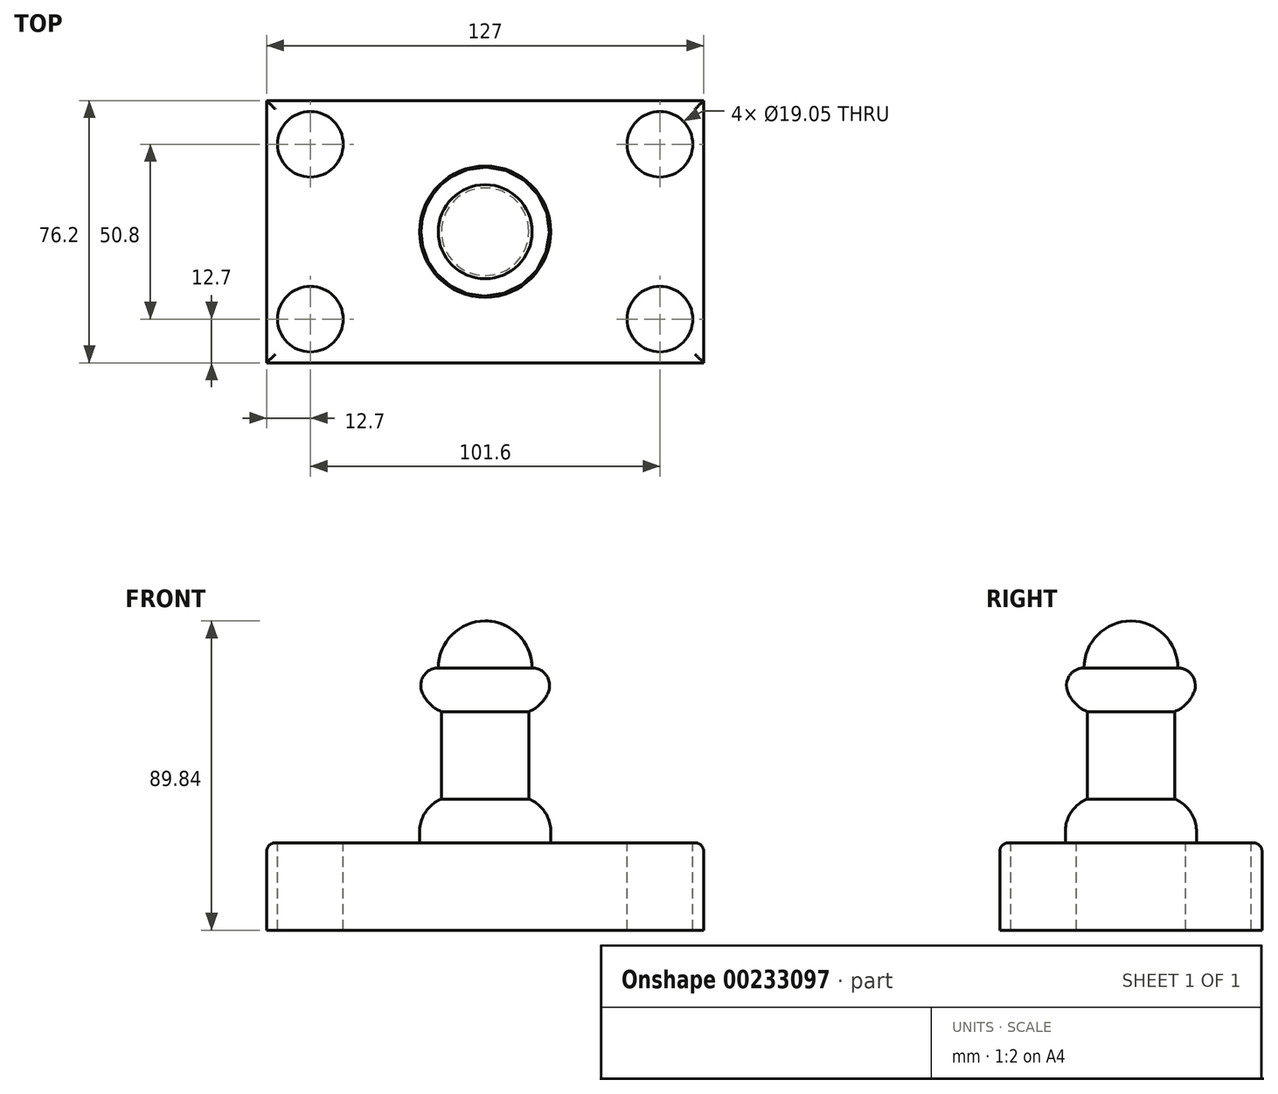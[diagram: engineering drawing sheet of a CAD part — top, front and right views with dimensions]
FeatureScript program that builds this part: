
annotation { "Feature Type Name" : "Feature", "Feature Type Description" : "" }
export const myFeature = defineFeature(function(context is Context, id is Id, definition is map)
    precondition{}
    {
        {
            var Q0;
            Q0=qCreatedBy(makeId("Top.planeOp"),FACE);
            var sketch = newSketch(context, id + "F0", { "sketchPlane" : qUnion([Q0])});
            skLineSegment(sketch, "E0.bottom", {"start": v(63.5, 38.1) * mm, "end": v(-63.5, 38.1) * mm});
            skLineSegment(sketch, "E0.top", {"start": v(63.5, -38.1) * mm, "end": v(-63.5, -38.1) * mm});
            skLineSegment(sketch, "E0.left", {"start": v(63.5, 38.1) * mm, "end": v(63.5, -38.1) * mm});
            skLineSegment(sketch, "E0.right", {"start": v(-63.5, 38.1) * mm, "end": v(-63.5, -38.1) * mm});
            skPoint(sketch, "E0.middle", {"position": v(0, 0) * mm});
            skSolve(sketch);
        }
        {
            var Q0;
            Q0=makeQuery(id+"F0.imprint","IMPRINT",FACE,{"disambiguationData":[TD([[makeQuery(id+"F0.imprint","IMPRINT",EDGE,{"derivedFrom":sQuery(id+"F0.wireOp",EDGE,"E0.bottom")}),1.0]])]});
            extrude(context, id + "F1", {"entities" : qUnion([Q0]), "depth" : 25.4 * mm});
        }
        {
            var Q0;
            Q0=makeQuery(id+"F1.opExtrude","CAP_FACE",FACE,{"disambiguationData":[OSD([sQuery(id+"F0.wireOp",EDGE,"E0.bottom"),sQuery(id+"F0.wireOp",EDGE,"E0.top"),sQuery(id+"F0.wireOp",EDGE,"E0.left"),sQuery(id+"F0.wireOp",EDGE,"E0.right")])],"isStart":false});
            var sketch = newSketch(context, id + "F2", { "sketchPlane" : qUnion([Q0])});
            skCircle(sketch, "E1", {"center": v(-50.8, 25.4) * mm, "radius": 9.53 * mm});
            skCircle(sketch, "E2", {"center": v(50.8, 25.4) * mm, "radius": 9.53 * mm});
            skCircle(sketch, "E3", {"center": v(50.8, -25.4) * mm, "radius": 9.53 * mm});
            skCircle(sketch, "E4", {"center": v(-50.8, -25.4) * mm, "radius": 9.53 * mm});
            skSolve(sketch);
        }
        {
            var Q0;
            Q0=sQuery(id+"F2.wireOp",VERTEX,"E1.center");
            var Q1;
            Q1=sQuery(id+"F2.wireOp",VERTEX,"E2.center");
            var Q2;
            Q2=sQuery(id+"F2.wireOp",VERTEX,"E4.center");
            var Q3;
            Q3=sQuery(id+"F2.wireOp",VERTEX,"E3.center");
            var Q4;
            Q4=makeQuery(id+"F1.opExtrude","SWEPT_BODY",BODY,{"disambiguationData":[OSD([sQuery(id+"F0.wireOp",EDGE,"E0.bottom"),sQuery(id+"F0.wireOp",EDGE,"E0.top"),sQuery(id+"F0.wireOp",EDGE,"E0.left"),sQuery(id+"F0.wireOp",EDGE,"E0.right")])]});
            hole(context, id + "F3", {"style" : HoleStyle.SIMPLE, "endStyle" : HoleEndStyle.THROUGH, "holeDiameter" : 19.05 * mm, "locations" : qUnion([Q0, Q1, Q2, Q3]), "scope" : qUnion([Q4]), "isTappedThrough" : true});
        }
        {
            var Q0;
            Q0=qCreatedBy(makeId("Front.planeOp"),FACE);
            var sketch = newSketch(context, id + "F4", { "sketchPlane" : qUnion([Q0])});
            skLineSegment(sketch, "E5.bottom", {"start": v(0, 25.4) * mm, "end": v(-19.05, 25.4) * mm});
            skLineSegment(sketch, "E5.top", {"start": v(0, 76.2) * mm, "end": v(-19.05, 76.2) * mm});
            skLineSegment(sketch, "E5.left", {"start": v(0, 25.4) * mm, "end": v(0, 76.2) * mm});
            skLineSegment(sketch, "E5.right", {"start": v(-19.05, 25.4) * mm, "end": v(-19.05, 76.2) * mm});
            skSolve(sketch);
        }
        {
            var Q0;
            Q0=makeQuery(id+"F4.imprint","IMPRINT",FACE,{"disambiguationData":[TD([[makeQuery(id+"F4.imprint","IMPRINT",EDGE,{"derivedFrom":sQuery(id+"F4.wireOp",EDGE,"E5.bottom")}),-1.0]])]});
            var Q1;
            Q1=sQuery(id+"F4.wireOp",EDGE,"E5.left");
            revolve(context, id + "F5", {"operationType" : NewBodyOperationType.ADD, "entities" : qUnion([Q0]), "axis" : qUnion([Q1]), "revolveType" : RevolveType.FULL});
        }
        {
            var Q0;
            Q0=qCreatedBy(makeId("Front.planeOp"),FACE);
            var sketch = newSketch(context, id + "F6", { "sketchPlane" : qUnion([Q0])});
            skLineSegment(sketch, "E6.bottom", {"start": v(-25.4, 63.5) * mm, "end": v(-12.7, 63.5) * mm});
            skLineSegment(sketch, "E6.top", {"start": v(-25.4, 38.1) * mm, "end": v(-12.7, 38.1) * mm});
            skLineSegment(sketch, "E6.left", {"start": v(-25.4, 63.5) * mm, "end": v(-25.4, 38.1) * mm});
            skLineSegment(sketch, "E6.right", {"start": v(-12.7, 63.5) * mm, "end": v(-12.7, 38.1) * mm});
            skLineSegment(sketch, "E7.bottom", {"start": v(-12.7, 63.5) * mm, "end": v(0, 63.5) * mm, "construction": true});
            skLineSegment(sketch, "E7.top", {"start": v(-12.7, 38.1) * mm, "end": v(0, 38.1) * mm, "construction": true});
            skLineSegment(sketch, "E7.left", {"start": v(-12.7, 63.5) * mm, "end": v(-12.7, 38.1) * mm, "construction": true});
            skLineSegment(sketch, "E7.right", {"start": v(0, 63.5) * mm, "end": v(0, 38.1) * mm, "construction": true});
            skSolve(sketch);
        }
        {
            var Q0;
            Q0=makeQuery(id+"F6.imprint","IMPRINT",FACE,{"disambiguationData":[TD([[makeQuery(id+"F6.imprint","IMPRINT",EDGE,{"derivedFrom":sQuery(id+"F6.wireOp",EDGE,"E6.bottom")}),-1.0]])]});
            var Q1;
            Q1=sQuery(id+"F6.wireOp",EDGE,"E7.right");
            revolve(context, id + "F7", {"operationType" : NewBodyOperationType.REMOVE, "entities" : qUnion([Q0]), "axis" : qUnion([Q1]), "revolveType" : RevolveType.FULL, "oppositeDirection" : true});
        }
        {
            var Q0;
            Q0=makeQuery(id+"F7.boolean.opBoolean","INTERSECT",EDGE,{"derivedFrom":[makeQuery(id+"F5.opRevolve","SWEPT_FACE",FACE,{"disambiguationData":[OSD([sQuery(id+"F4.wireOp",EDGE,"E5.right")])]}),makeQuery(id+"F7.opRevolve","SWEPT_FACE",FACE,{"disambiguationData":[OSD([sQuery(id+"F6.wireOp",EDGE,"E6.top")])]})]});
            var Q1;
            Q1=makeQuery(id+"F7.boolean.opBoolean","INTERSECT",EDGE,{"derivedFrom":[makeQuery(id+"F5.opRevolve","SWEPT_FACE",FACE,{"disambiguationData":[OSD([sQuery(id+"F4.wireOp",EDGE,"E5.right")])]}),makeQuery(id+"F7.opRevolve","SWEPT_FACE",FACE,{"disambiguationData":[OSD([sQuery(id+"F6.wireOp",EDGE,"E6.bottom")])]})]});
            fillet(context, id + "F8", {"entities" : qUnion([Q0, Q1]), "radius" : 10.16 * mm, "tangentPropagation" : true, "allowEdgeOverflow" : false});
        }
        {
            var Q0;
            Q0=makeQuery(id+"F1.opExtrude","CAP_EDGE",EDGE,{"disambiguationData":[OSD([sQuery(id+"F0.wireOp",EDGE,"E0.bottom")])],"isStart":false});
            var Q1;
            Q1=makeQuery(id+"F1.opExtrude","CAP_EDGE",EDGE,{"disambiguationData":[OSD([sQuery(id+"F0.wireOp",EDGE,"E0.left")])],"isStart":false});
            var Q2;
            Q2=makeQuery(id+"F1.opExtrude","CAP_EDGE",EDGE,{"disambiguationData":[OSD([sQuery(id+"F0.wireOp",EDGE,"E0.top")])],"isStart":false});
            var Q3;
            Q3=makeQuery(id+"F1.opExtrude","CAP_EDGE",EDGE,{"disambiguationData":[OSD([sQuery(id+"F0.wireOp",EDGE,"E0.right")])],"isStart":false});
            fillet(context, id + "F9", {"entities" : qUnion([Q0, Q1, Q2, Q3]), "radius" : 2.54 * mm, "tangentPropagation" : true, "allowEdgeOverflow" : false});
        }
        {
            var Q0;
            Q0=makeQuery(id+"F5.opRevolve","SWEPT_EDGE",EDGE,{"disambiguationData":[OSD([sQuery(id+"F4.wireOp",EDGE,"E5.top"),sQuery(id+"F4.wireOp",EDGE,"E5.right")])]});
            fillet(context, id + "F10", {"entities" : qUnion([Q0]), "radius" : 5.08 * mm, "tangentPropagation" : true, "allowEdgeOverflow" : false});
        }
        {
            var Q0;
            Q0=qCreatedBy(makeId("Front.planeOp"),FACE);
            var sketch = newSketch(context, id + "F11", { "sketchPlane" : qUnion([Q0])});
            skArc(sketch, "E8", {"start": v(0, 89.84) * mm, "mid": v(-9.71, 85.78) * mm, "end": v(-13.64, 76.01) * mm});
            skLineSegment(sketch, "E9", {"start": v(0, 76.2) * mm, "end": v(0, 89.84) * mm, "construction": true});
            skLineSegment(sketch, "E10", {"start": v(-13.64, 76.01) * mm, "end": v(0, 76.2) * mm});
            skLineSegment(sketch, "E11", {"start": v(0, 89.84) * mm, "end": v(0, 76.2) * mm});
            skSolve(sketch);
        }
        {
            var Q0;
            Q0=makeQuery(id+"F11.imprint","IMPRINT",FACE,{"disambiguationData":[TD([[makeQuery(id+"F11.imprint","IMPRINT",EDGE,{"derivedFrom":sQuery(id+"F11.wireOp",EDGE,"E8")}),1.0]])]});
            var Q1;
            Q1=sQuery(id+"F11.wireOp",EDGE,"E11");
            revolve(context, id + "F12", {"operationType" : NewBodyOperationType.ADD, "entities" : qUnion([Q0]), "axis" : qUnion([Q1]), "revolveType" : RevolveType.FULL});
        }
    });
